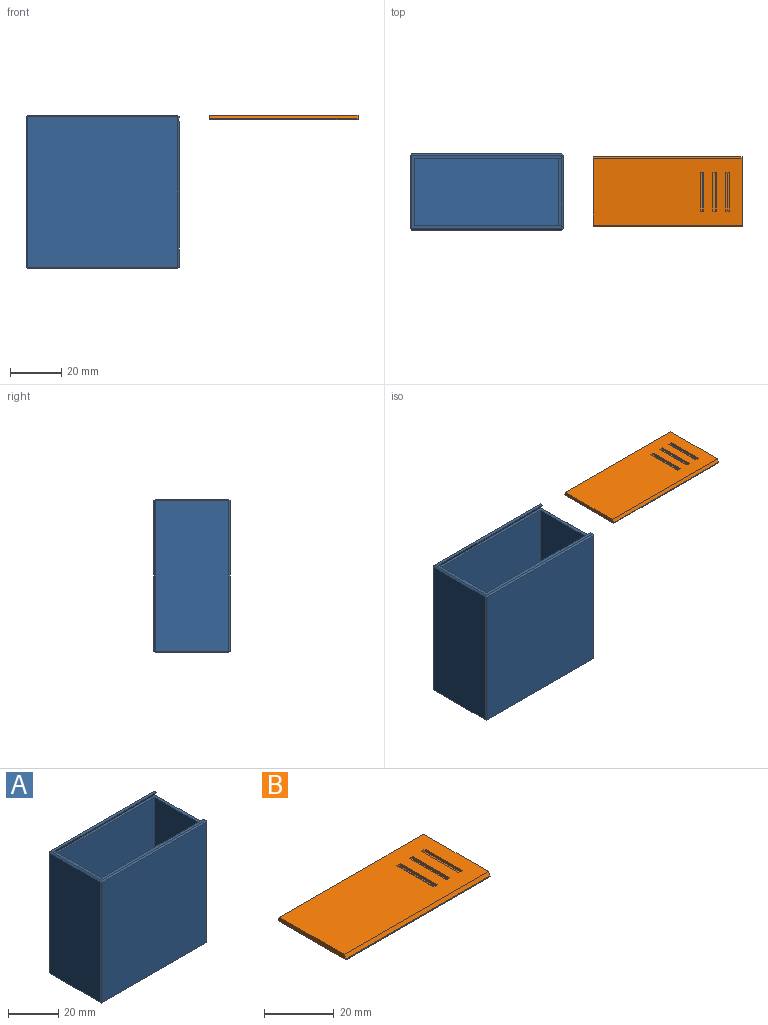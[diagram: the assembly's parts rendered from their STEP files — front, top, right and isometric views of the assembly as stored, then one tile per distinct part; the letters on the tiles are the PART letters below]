
ASSEMBLY  parts=2 mates=1
PART A: 40 faces, bbox 60x30x60 mm
  f0: plane 0.28x0.16mm, normal (1,0,0), area 0mm2, adj f17,f23,f24
  f1: plane 0.28x0.16mm, normal (1,0,0), area 0mm2, adj f18,f25,f26
  f2: plane 57x28.8mm, normal (1,0,0), area 1641.6mm2, adj f16,f20,f23,f26
  f3: plane 56.4x56.4mm, normal (0,1,0), area 3181mm2, adj f8,f11,f12,f13
  f4: plane 56.4x56.4mm, normal (0,-1,0), area 3181mm2, adj f8,f11,f12,f13
  f5: plane 58.8x58.8mm, normal (0,1,0), area 3457.4mm2, adj f22,f23,f33,f34
  f6: plane 58.8x28.8mm, normal (-1,0,0), area 1693.4mm2, adj f28,f33,f36,f39
  f7: plane 58.8x58.8mm, normal (0,-1,0), area 3457.4mm2, adj f26,f27,f35,f36
  f8: plane 58.2x28.48mm, normal (1,0,0), area 1538.4mm2, adj f3,f4,f9,f11,f13,f14,f15
  f9: plane 58.8x28.8mm, normal (0,0,1), area 172.8mm2, adj f8,f14,f15,f24,f25,f34,f35,f39
  f10: plane 58.8x28.8mm, normal (0,0,-1), area 1693.4mm2, adj f16,f22,f27,f28
  f11: plane 56.4x26.4mm, normal (0,0,1), area 1489mm2, adj f3,f4,f8,f12
  f12: plane 56.4x26.4mm, normal (-1,0,0), area 1489mm2, adj f3,f4,f11,f13
  f13: plane 57.6x28.48mm, normal (0,0,1), area 151.4mm2, adj f3,f4,f8,f12,f14,f15,f20
  f14: plane 57.6x1.8mm, normal (0,0.87,-0.5), area 119.7mm2, adj f8,f9,f13,f18
  f15: plane 57.6x1.8mm, normal (0,-0.87,-0.5), area 119.7mm2, adj f8,f9,f13,f17
  f16: plane 28.8x0.6mm, normal (0.71,0,-0.71), area 24.4mm2, adj f2,f10,f19,f21
  f17: plane 2.08x1.52mm, normal (0.71,-0.61,-0.35), area 1.4mm2, adj f0,f15,f20,f23,f24
  f18: plane 2.08x1.52mm, normal (0.71,0.61,-0.35), area 1.4mm2, adj f1,f14,f20,f25,f26
  f19: plane 0.6x0.6mm, normal (0.58,0.58,-0.58), area 0.3mm2, adj f16,f22,f23
  f20: plane 29.44x0.6mm, normal (0.71,0,0.71), area 24.6mm2, adj f2,f13,f17,f18,f23,f26
  f21: plane 0.6x0.6mm, normal (0.58,-0.58,-0.58), area 0.3mm2, adj f16,f26,f27
  f22: plane 58.8x0.6mm, normal (0,0.71,-0.71), area 49.9mm2, adj f5,f10,f19,f29
  f23: plane 58.8x0.6mm, normal (0.71,0.71,0), area 49.5mm2, adj f0,f2,f5,f17,f19,f20,f30
  f24: plane 1.2x0.6mm, normal (0.71,0,0.71), area 0.6mm2, adj f0,f9,f17,f30
  f25: plane 1.2x0.6mm, normal (0.71,0,0.71), area 0.6mm2, adj f1,f9,f18,f31
  f26: plane 58.8x0.6mm, normal (0.71,-0.71,0), area 49.5mm2, adj f1,f2,f7,f18,f20,f21,f31
  f27: plane 58.8x0.6mm, normal (0,-0.71,-0.71), area 49.9mm2, adj f7,f10,f21,f32
  f28: plane 28.8x0.6mm, normal (-0.71,0,-0.71), area 24.4mm2, adj f6,f10,f29,f32
  f29: plane 0.6x0.6mm, normal (-0.58,0.58,-0.58), area 0.3mm2, adj f22,f28,f33
  f30: plane 0.6x0.6mm, normal (0.58,0.58,0.58), area 0.3mm2, adj f23,f24,f34
  f31: plane 0.6x0.6mm, normal (0.58,-0.58,0.58), area 0.3mm2, adj f25,f26,f35
  f32: plane 0.6x0.6mm, normal (-0.58,-0.58,-0.58), area 0.3mm2, adj f27,f28,f36
  f33: plane 58.8x0.6mm, normal (-0.71,0.71,0), area 49.9mm2, adj f5,f6,f29,f37
  f34: plane 58.8x0.6mm, normal (0,0.71,0.71), area 49.9mm2, adj f5,f9,f30,f37
  f35: plane 58.8x0.6mm, normal (0,-0.71,0.71), area 49.9mm2, adj f7,f9,f31,f38
  f36: plane 58.8x0.6mm, normal (-0.71,-0.71,0), area 49.9mm2, adj f6,f7,f32,f38
  f37: plane 0.6x0.6mm, normal (-0.58,0.58,0.58), area 0.3mm2, adj f33,f34,f39
  f38: plane 0.6x0.6mm, normal (-0.58,-0.58,0.58), area 0.3mm2, adj f35,f36,f39
  f39: plane 28.8x0.6mm, normal (-0.71,0,0.71), area 24.4mm2, adj f6,f9,f37,f38
PART B: 25 faces, bbox 58.2x27.5x1.8 mm
  f0: plane 58.2x26mm, normal (0,0,1), area 1450.2mm2, adj f2,f3,f4,f5,f6,f7,f8,f10
  f1: plane 57.51x26.88mm, normal (0,0,-1), area 1545.7mm2, adj f21,f22,f23,f24
  f2: plane 58.2x1.28mm, normal (0,0.87,0.5), area 86mm2, adj f0,f4,f5,f23
  f3: plane 58.2x1.28mm, normal (0,-0.87,0.5), area 86mm2, adj f0,f4,f5,f22
  f4: plane 27.48x1.45mm, normal (1,0,0), area 39mm2, adj f0,f2,f3,f22,f23,f24
  f5: plane 27.48x1.45mm, normal (-1,0,0), area 39mm2, adj f0,f2,f3,f21,f22,f23
  f6: plane 1.4x0.9mm, normal (0,-1,0), area 0.9mm2, adj f0,f8,f9,f20
  f7: plane 1.4x0.9mm, normal (0,1,0), area 0.9mm2, adj f0,f8,f9,f20
  f8: plane 15x0.9mm, normal (-1,0,0), area 13.5mm2, adj f0,f6,f7,f9
  f9: plane 15x0.5mm, normal (0,0,1), area 7.5mm2, adj f6,f7,f8,f20
  f10: plane 1.4x0.9mm, normal (0,-1,0), area 0.9mm2, adj f0,f12,f13,f19
  f11: plane 1.4x0.9mm, normal (0,1,0), area 0.9mm2, adj f0,f12,f13,f19
  f12: plane 15x0.9mm, normal (-1,0,0), area 13.5mm2, adj f0,f10,f11,f13
  f13: plane 15x0.5mm, normal (0,0,1), area 7.5mm2, adj f10,f11,f12,f19
  f14: plane 1.4x0.9mm, normal (0,-1,0), area 0.9mm2, adj f0,f16,f17,f18
  f15: plane 1.4x0.9mm, normal (0,1,0), area 0.9mm2, adj f0,f16,f17,f18
  f16: plane 15x0.9mm, normal (-1,0,0), area 13.5mm2, adj f0,f14,f15,f17
  f17: plane 15x0.5mm, normal (0,0,1), area 7.5mm2, adj f14,f15,f16,f18
  f18: plane 15x0.9mm, normal (0.71,0,0.71), area 19.1mm2, adj f0,f14,f15,f17
  f19: plane 15x0.9mm, normal (0.71,0,0.71), area 19.1mm2, adj f0,f10,f11,f13
  f20: plane 15x0.9mm, normal (0.71,0,0.71), area 19.1mm2, adj f0,f6,f7,f9
  f21: plane 27.28x0.35mm, normal (-0.71,0,-0.71), area 13.3mm2, adj f1,f5,f22,f23
  f22: plane 58.2x0.52mm, normal (0,-0.87,-0.5), area 34.8mm2, adj f1,f3,f4,f5,f21,f24
  f23: plane 58.2x0.52mm, normal (0,0.87,-0.5), area 34.8mm2, adj f1,f2,f4,f5,f21,f24
  f24: plane 27.28x0.35mm, normal (0.71,0,-0.71), area 13.3mm2, adj f1,f4,f22,f23
PLACE A t=(-30,-15,0)mm
PLACE B t=(-19.97,-15,58.2)mm
MATE slider B.f5 <-> A.f8  axis (-1,0,0) through (41.83,0,60)mm
